# Revit family: Disc XL
name_source: partatom
category: Мебель
revit_build: Autodesk Revit 2017 (Build: 20160225_1515(x64)
units: mm (PartAtom-declared; Revit-internal decimal feet)

## family parameters
Всегда вертикально = Да
Заголовок OmniClass = General Furniture and Specialties
На основе рабочей плоскости = Нет
Номер OmniClass = 23.40.20.00
Общий = Нет
При загрузке вырезать с полостями = Нет
Точка расчета площади = Нет

## types (6) — shared parameters
Table Leg = Skandiform Chrome
Table Top = Skandiform Wood Oak
Изготовитель = Skandiform AB
Ключевая пометка = XBE.1
Комментарии к типоразмеру = Created by Astacus AB
Описание = Table tops in birch, oak veneer or white laminate F2274.Chassis straight legs in silver lacquer or chromium. Adjustable floor protectors

## per-type parameters (varying)
| type | Disc | Leg | URL |
| HB-920 | HB-920-Disc | Straight legs 2pc small | http://file-system.ru |
| HB-921 | HB-921-Disc | Straight legs 3pc small | http://www.biminfo.se |
| HB-922 | HB-922-Disc | Straight legs 4pc small | http://www.biminfo.se |
| HB-1920 | HB-920-Disc | T legs 2pc small | http://www.biminfo.se |
| HB-1921 | HB-921-Disc | T legs 3pc small | http://www.biminfo.se |
| HB-1922 | HB-922-Disc | T legs 4pc small | http://www.biminfo.se |

note: column(s) folded — value = type name in every type: Группа модели

## geometry (parser evidence)
native form markers: Blend x30, Sweep x17
no freeform markers — native parametric forms only
